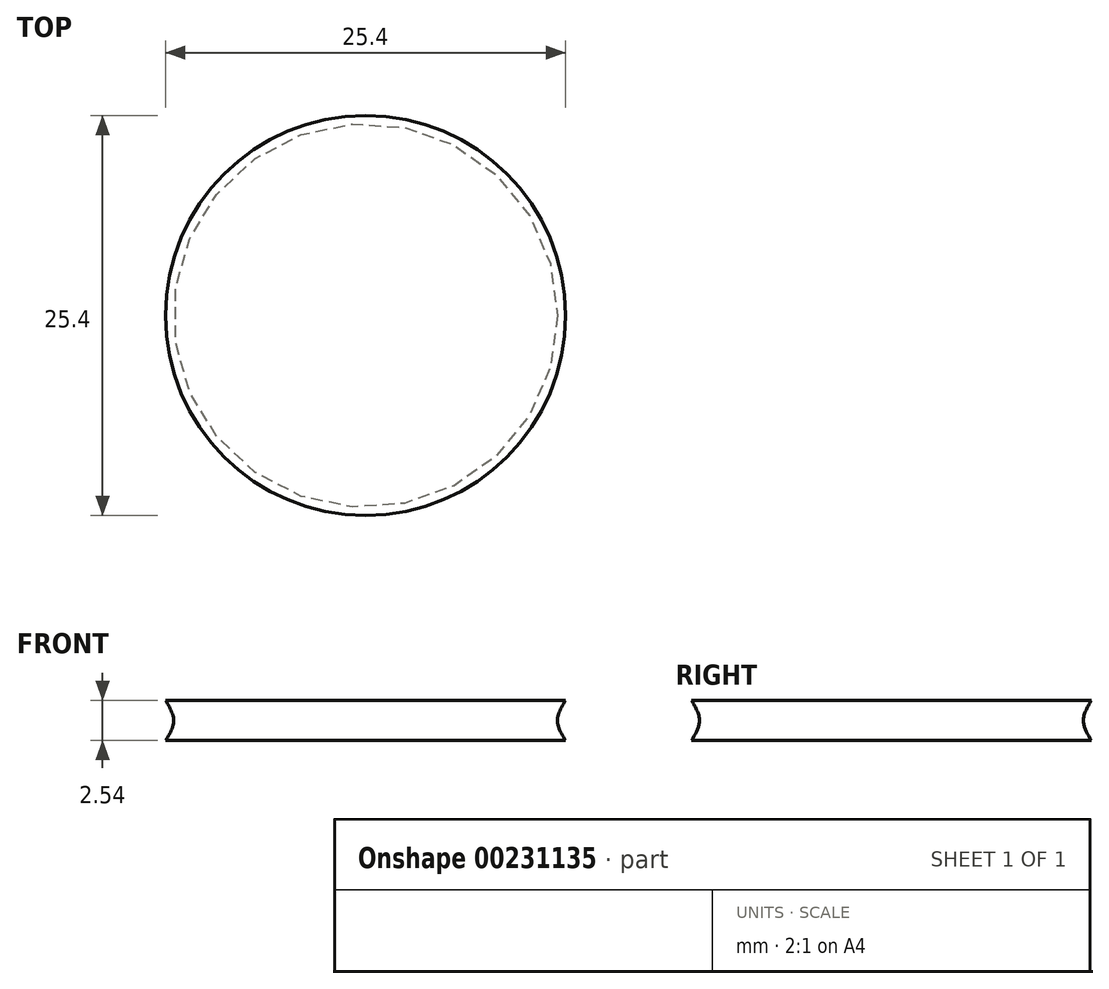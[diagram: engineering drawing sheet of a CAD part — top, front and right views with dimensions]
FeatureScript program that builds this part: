
annotation { "Feature Type Name" : "Feature", "Feature Type Description" : "" }
export const myFeature = defineFeature(function(context is Context, id is Id, definition is map)
    precondition{}
    {
        {
            var Q0;
            Q0=qCreatedBy(makeId("Front.planeOp"),FACE);
            var sketch = newSketch(context, id + "F0", { "sketchPlane" : qUnion([Q0])});
            skLineSegment(sketch, "E0", {"start": v(0, 1.27) * mm, "end": v(12.7, 1.27) * mm});
            skLineSegment(sketch, "E1", {"start": v(0, -1.27) * mm, "end": v(12.7, -1.27) * mm});
            skFitSpline(sketch, "E2", {"points": [v(12.7, 1.27) * mm, v(12.2, 0) * mm, v(12.7, -1.27) * mm], "startDerivative": vector(-1.52, -2.58) * mm, "endDerivative": vector(1.66, -2.5) * mm});
            skLineSegment(sketch, "E3", {"start": v(0, 1.27) * mm, "end": v(0, -1.27) * mm});
            skSolve(sketch);
        }
        {
            var Q0;
            Q0 = qSketchRegion(id + "F0", true);
            var Q1;
            Q1=sQuery(id+"F0.wireOp",EDGE,"E3");
            revolve(context, id + "F1", {"entities" : qUnion([Q0]), "axis" : qUnion([Q1]), "revolveType" : RevolveType.FULL});
        }
    });
